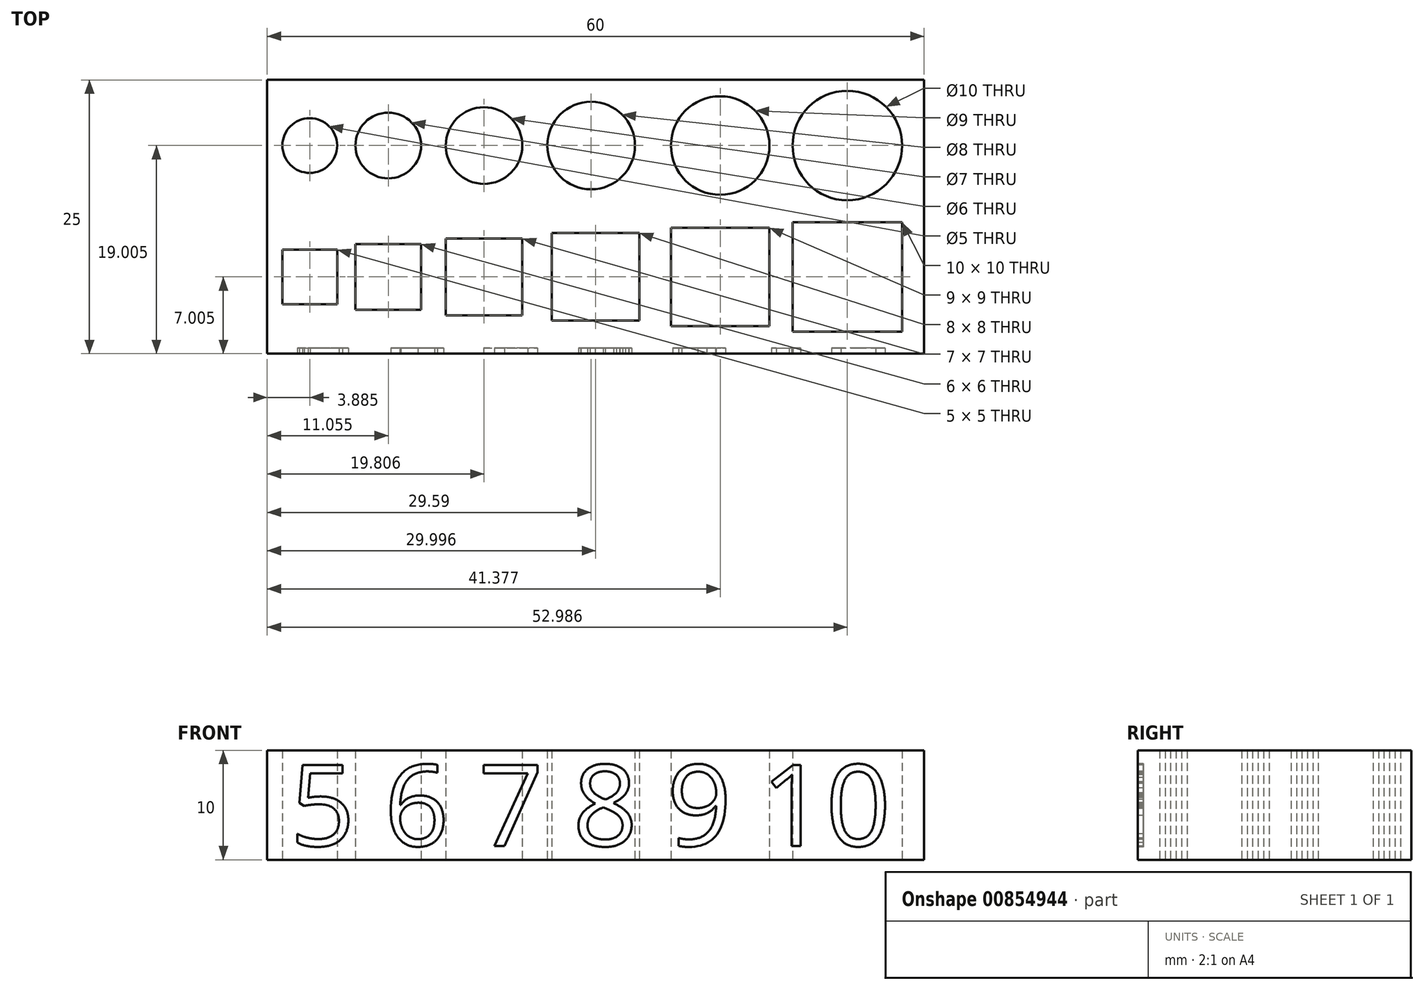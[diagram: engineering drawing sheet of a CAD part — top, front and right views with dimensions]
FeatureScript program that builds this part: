
annotation { "Feature Type Name" : "Feature", "Feature Type Description" : "" }
export const myFeature = defineFeature(function(context is Context, id is Id, definition is map)
    precondition{}
    {
        {
            var Q0;
            Q0=qCreatedBy(makeId("Top.planeOp"),FACE);
            var sketch = newSketch(context, id + "F0", { "sketchPlane" : qUnion([Q0])});
            skLineSegment(sketch, "E0.bottom", {"start": v(30.4, 12.21) * mm, "end": v(-29.6, 12.21) * mm});
            skLineSegment(sketch, "E0.top", {"start": v(30.4, -12.79) * mm, "end": v(-29.6, -12.79) * mm});
            skLineSegment(sketch, "E0.left", {"start": v(30.4, 12.21) * mm, "end": v(30.4, -12.79) * mm});
            skLineSegment(sketch, "E0.right", {"start": v(-29.6, 12.21) * mm, "end": v(-29.6, -12.79) * mm});
            skCircle(sketch, "E1", {"center": v(-25.7, 6.21) * mm, "radius": 2.5 * mm});
            skCircle(sketch, "E2", {"center": v(-18.53, 6.21) * mm, "radius": 3 * mm});
            skCircle(sketch, "E3", {"center": v(-9.78, 6.21) * mm, "radius": 3.5 * mm});
            skCircle(sketch, "E4", {"center": v(0, 6.21) * mm, "radius": 4 * mm});
            skCircle(sketch, "E5", {"center": v(11.79, 6.21) * mm, "radius": 4.5 * mm});
            skCircle(sketch, "E6", {"center": v(23.4, 6.21) * mm, "radius": 5 * mm});
            skLineSegment(sketch, "E7", {"start": v(23.4, 6.21) * mm, "end": v(-29.6, 6.21) * mm, "construction": true});
            skLineSegment(sketch, "E8", {"start": v(-29.6, -5.79) * mm, "end": v(30.4, -5.79) * mm, "construction": true});
            skPoint(sketch, "E9", {"position": v(-25.7, -5.79) * mm});
            skPoint(sketch, "E10", {"position": v(-18.53, -5.79) * mm});
            skPoint(sketch, "E11", {"position": v(-9.78, -5.79) * mm});
            skPoint(sketch, "E12", {"position": v(0.4, -5.79) * mm});
            skPoint(sketch, "E13", {"position": v(11.79, -5.79) * mm});
            skPoint(sketch, "E14", {"position": v(23.4, -5.79) * mm});
            skLineSegment(sketch, "E15.bottom", {"start": v(-23.2, -3.29) * mm, "end": v(-28.2, -3.29) * mm});
            skLineSegment(sketch, "E15.top", {"start": v(-23.2, -8.29) * mm, "end": v(-28.2, -8.29) * mm});
            skLineSegment(sketch, "E15.left", {"start": v(-23.2, -3.29) * mm, "end": v(-23.2, -8.29) * mm});
            skLineSegment(sketch, "E15.right", {"start": v(-28.2, -3.29) * mm, "end": v(-28.2, -8.29) * mm});
            skLineSegment(sketch, "E16.bottom", {"start": v(-15.53, -2.79) * mm, "end": v(-21.53, -2.79) * mm});
            skLineSegment(sketch, "E16.top", {"start": v(-15.53, -8.79) * mm, "end": v(-21.53, -8.79) * mm});
            skLineSegment(sketch, "E16.left", {"start": v(-15.53, -2.79) * mm, "end": v(-15.53, -8.79) * mm});
            skLineSegment(sketch, "E16.right", {"start": v(-21.53, -2.79) * mm, "end": v(-21.53, -8.79) * mm});
            skLineSegment(sketch, "E17.bottom", {"start": v(-6.28, -2.29) * mm, "end": v(-13.28, -2.29) * mm});
            skLineSegment(sketch, "E17.top", {"start": v(-6.28, -9.29) * mm, "end": v(-13.28, -9.29) * mm});
            skLineSegment(sketch, "E17.left", {"start": v(-6.28, -2.29) * mm, "end": v(-6.28, -9.29) * mm});
            skLineSegment(sketch, "E17.right", {"start": v(-13.28, -2.29) * mm, "end": v(-13.28, -9.29) * mm});
            skLineSegment(sketch, "E18.bottom", {"start": v(4.4, -1.79) * mm, "end": v(-3.6, -1.79) * mm});
            skLineSegment(sketch, "E18.top", {"start": v(4.4, -9.79) * mm, "end": v(-3.6, -9.79) * mm});
            skLineSegment(sketch, "E18.left", {"start": v(4.4, -1.79) * mm, "end": v(4.4, -9.79) * mm});
            skLineSegment(sketch, "E18.right", {"start": v(-3.6, -1.79) * mm, "end": v(-3.6, -9.79) * mm});
            skLineSegment(sketch, "E19.bottom", {"start": v(16.29, -1.29) * mm, "end": v(7.29, -1.29) * mm});
            skLineSegment(sketch, "E19.top", {"start": v(16.29, -10.29) * mm, "end": v(7.29, -10.29) * mm});
            skLineSegment(sketch, "E19.left", {"start": v(16.29, -1.29) * mm, "end": v(16.29, -10.29) * mm});
            skLineSegment(sketch, "E19.right", {"start": v(7.29, -1.29) * mm, "end": v(7.29, -10.29) * mm});
            skLineSegment(sketch, "E20.bottom", {"start": v(28.4, -0.79) * mm, "end": v(18.4, -0.79) * mm});
            skLineSegment(sketch, "E20.top", {"start": v(28.4, -10.79) * mm, "end": v(18.4, -10.79) * mm});
            skLineSegment(sketch, "E20.left", {"start": v(28.4, -0.79) * mm, "end": v(28.4, -10.79) * mm});
            skLineSegment(sketch, "E20.right", {"start": v(18.4, -0.79) * mm, "end": v(18.4, -10.79) * mm});
            skSolve(sketch);
        }
        {
            var Q0;
            Q0=makeQuery(id+"F0.imprint","IMPRINT",FACE,{"disambiguationData":[TD([[makeQuery(id+"F0.imprint","IMPRINT",EDGE,{"derivedFrom":sQuery(id+"F0.wireOp",EDGE,"E0.bottom")}),1.0]])]});
            extrude(context, id + "F1", {"entities" : qUnion([Q0]), "depth" : 10 * mm, "offsetDistance" : 25 * mm});
        }
        {
            var Q0;
            Q0=makeQuery(id+"F1.opExtrude","SWEPT_FACE",FACE,{"disambiguationData":[OSD([sQuery(id+"F0.wireOp",EDGE,"E0.top")])]});
            var sketch = newSketch(context, id + "F2", { "sketchPlane" : qUnion([Q0])});
            skText(sketch, "E21", { "text": "5 6 7 8 9 10", "fontName": "OpenSans-Regular.ttf"});
            const initialGuessF2  = {"E21": [-0.0275, 0.00127, 1, 0, 0.00745]};
            skSetInitialGuess(sketch, initialGuessF2);
            skSolve(sketch);
        }
        {
            var Q0;
            Q0 = qSketchRegion(id + "F2", true);
            extrude(context, id + "F3", {"entities" : qUnion([Q0]), "operationType" : NewBodyOperationType.REMOVE, "oppositeDirection" : true, "depth" : 0.5 * mm, "offsetDistance" : 25 * mm});
        }
    });
